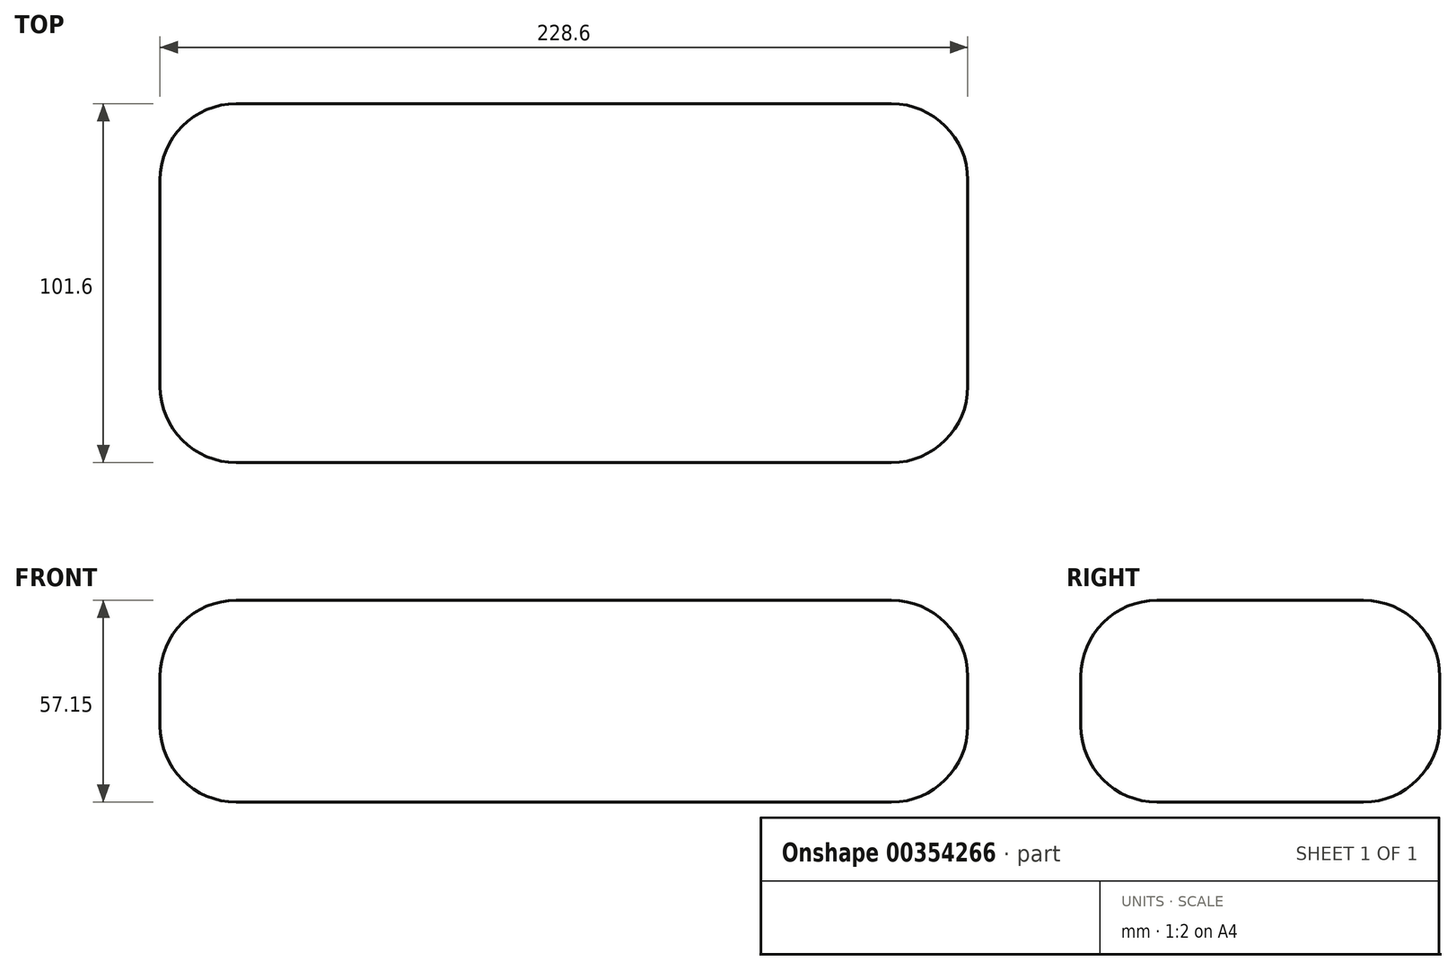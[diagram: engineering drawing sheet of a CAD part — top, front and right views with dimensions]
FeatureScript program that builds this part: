
annotation { "Feature Type Name" : "Feature", "Feature Type Description" : "" }
export const myFeature = defineFeature(function(context is Context, id is Id, definition is map)
    precondition{}
    {
        {
            var Q0;
            Q0=qCreatedBy(makeId("Front.planeOp"),FACE);
            var sketch = newSketch(context, id + "F0", { "sketchPlane" : qUnion([Q0])});
            skLineSegment(sketch, "E0", {"start": v(-36.2, -21.8) * mm, "end": v(-36.2, 35.35) * mm});
            skLineSegment(sketch, "E1", {"start": v(-36.2, 35.35) * mm, "end": v(192.4, 35.35) * mm});
            skLineSegment(sketch, "E2", {"start": v(192.4, 35.35) * mm, "end": v(192.4, -21.8) * mm});
            skLineSegment(sketch, "E3", {"start": v(192.4, -21.8) * mm, "end": v(-36.2, -21.8) * mm});
            skSolve(sketch);
        }
        {
            var Q0;
            Q0=makeQuery(id+"F0.imprint","IMPRINT",FACE,{"disambiguationData":[TD([[makeQuery(id+"F0.imprint","IMPRINT",EDGE,{"derivedFrom":sQuery(id+"F0.wireOp",EDGE,"E0")}),-1.0]])]});
            extrude(context, id + "F1", {"entities" : qUnion([Q0]), "endBound" : BoundingType.SYMMETRIC, "depth" : 101.6 * mm});
        }
        {
            var Q0;
            Q0=makeQuery(id+"F1.opExtrude","SWEPT_EDGE",EDGE,{"disambiguationData":[OSD([sQuery(id+"F0.wireOp",EDGE,"E1"),sQuery(id+"F0.wireOp",EDGE,"E2")])]});
            var Q1;
            Q1=makeQuery(id+"F1.opExtrude","CAP_EDGE",EDGE,{"disambiguationData":[OSD([sQuery(id+"F0.wireOp",EDGE,"E1")])],"isStart":false});
            var Q2;
            Q2=makeQuery(id+"F1.opExtrude","CAP_EDGE",EDGE,{"disambiguationData":[OSD([sQuery(id+"F0.wireOp",EDGE,"E2")])],"isStart":false});
            var Q3;
            Q3=makeQuery(id+"F1.opExtrude","CAP_EDGE",EDGE,{"disambiguationData":[OSD([sQuery(id+"F0.wireOp",EDGE,"E0")])],"isStart":false});
            var Q4;
            Q4=makeQuery(id+"F1.opExtrude","SWEPT_EDGE",EDGE,{"disambiguationData":[OSD([sQuery(id+"F0.wireOp",EDGE,"E0"),sQuery(id+"F0.wireOp",EDGE,"E1")])]});
            var Q5;
            Q5=makeQuery(id+"F1.opExtrude","CAP_EDGE",EDGE,{"disambiguationData":[OSD([sQuery(id+"F0.wireOp",EDGE,"E1")])],"isStart":true});
            var Q6;
            Q6=makeQuery(id+"F1.opExtrude","CAP_EDGE",EDGE,{"disambiguationData":[OSD([sQuery(id+"F0.wireOp",EDGE,"E2")])],"isStart":true});
            var Q7;
            Q7=makeQuery(id+"F1.opExtrude","CAP_EDGE",EDGE,{"disambiguationData":[OSD([sQuery(id+"F0.wireOp",EDGE,"E0")])],"isStart":true});
            var Q8;
            Q8=makeQuery(id+"F1.opExtrude","SWEPT_EDGE",EDGE,{"disambiguationData":[OSD([sQuery(id+"F0.wireOp",EDGE,"E2"),sQuery(id+"F0.wireOp",EDGE,"E3")])]});
            var Q9;
            Q9=makeQuery(id+"F1.opExtrude","CAP_EDGE",EDGE,{"disambiguationData":[OSD([sQuery(id+"F0.wireOp",EDGE,"E3")])],"isStart":false});
            var Q10;
            Q10=makeQuery(id+"F1.opExtrude","CAP_EDGE",EDGE,{"disambiguationData":[OSD([sQuery(id+"F0.wireOp",EDGE,"E3")])],"isStart":true});
            var Q11;
            Q11=makeQuery(id+"F1.opExtrude","SWEPT_EDGE",EDGE,{"disambiguationData":[OSD([sQuery(id+"F0.wireOp",EDGE,"E0"),sQuery(id+"F0.wireOp",EDGE,"E3")])]});
            fillet(context, id + "F2", {"entities" : qUnion([Q0, Q1, Q2, Q3, Q4, Q5, Q6, Q7, Q8, Q9, Q10, Q11]), "radius" : 21.59 * mm, "tangentPropagation" : true, "allowEdgeOverflow" : false});
        }
    });
